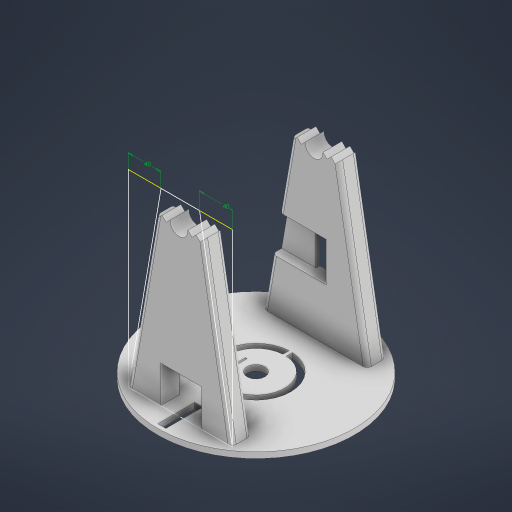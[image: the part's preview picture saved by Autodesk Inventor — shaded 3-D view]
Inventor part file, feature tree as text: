
AUTODESK INVENTOR PART (.ipt)
format: ipt  version: 2023 (Build 270158030, 158C)  size: 431,104 bytes
history: native  units: in
note: dims shown in document units (in); Inventor stores cm internally (conversion verified against a paired STEP export)
features: sketch x16, extrude x14, fillet x2, split x1
ambient origin geometry x8: Origin, YZ Plane, XZ Plane, XY Plane, X Axis, Y Axis, Z Axis, Center Point
bodies: Solid1 (feature_tree)
feature tree (33):
  extrude  "Extrusion1"  Depth=0.2756in TaperAngle=0.0deg
  extrude  "Extrusion2"  Depth=0.2756in TaperAngle=0.0deg
  sketch  "Sketch4"  dims[d10=5.0in d11=0.9055in]
  sketch  "Sketch5"  dims[d12=0.1969in d13=5.0in d14=0.9055in]
  sketch  "Sketch6"  dims[d16=2.7953in d17=9.0551in d18=0.0in]
  extrude  "Extrusion4"  Depth=0.9055in
  extrude  "Extrusion5"  Depth=0.9055in
  extrude  "Extrusion6"  Depth=9.0551in TaperAngle=0.0deg
  extrude  "Extrusion7"  Depth=1.9685in
  sketch  "Sketch9"  dims[d28=1.5748in d29=1.5748in]
  sketch  "Sketch10"  dims[d30=1.5748in d31=1.5748in]
  extrude  "Extrusion8"  Depth=1.7717in
  fillet  "Fillet1"  Radius=9.0551in
  fillet  "Fillet2"  Radius=7.2835in
  extrude  "Extrusion9"  Depth=1.5748in
  extrude  "Extrusion10"  Depth=1.5748in
  sketch  "Sketch16"  dims[d37=10.9085in d38=0.0in d39=0.2756in d40=0.0in]
  extrude  "Extrusion13"  Depth=0.1969in
  extrude  "Extrusion14"  Depth=0.1969in
  extrude  "Extrusion16"  Depth=0.2756in TaperAngle=0.0deg
  extrude  "Extrusion17"  Depth=0.3937in
  extrude  "Extrusion18"  Depth=0.3937in TaperAngle=0.0deg
  split  "Split1"
  sketch  "Sketch1"  dims[d0=9.4488in d1=0.2756in d2=0.0in]
  sketch  "Sketch2"  dims[d3=0.8583in d4=0.2756in d5=0.0in]
  sketch  "Sketch7"  dims[d19=9.0551in d20=0.0in d21=1.9685in]
  sketch  "Sketch8"  dims[d22=1.7717in d23=0.8858in d24=9.0551in d25=0.0in d26=7.2835in d27=0.0in]
  sketch  "Sketch11"  dims[d32=10.9085in d33=0.0in d34=0.1969in]
  sketch  "Sketch12"  dims[d35=0.1969in d36=0.8583in]
  sketch  "Sketch20"  dims[d51=1.7717in d52=0.3937in]
  sketch  "Sketch21"  dims[d53=2.7559in d54=0.3937in d55=0.0in]
  sketch  "Sketch22"  dims[d57=2.9528in]
  sketch  "Sketch23"  dims[d58=1.9685in d59=0.9449in d60=0.5118in d61=1.5026in d62=0.6299in d63=0.0in d66=2.7559in d67=3.3465in d68=0.0787in d69=0.0787in d70=0.0787in d71=0.4469in d72=0.0in d73=0.3346in d74=0.3346in d75=0.0787in d76=0.4469in d77=0.0in d80=1.9685in d81=1.8898in d82=0.4469in d83=0.0in d84=0.2756in d85=45.0deg d86=0.2756in d87=135.0deg d88=0.2756in d89=135.0deg d90=0.2756in d91=135.0deg d92=0.0984in d93=135.0deg d94=0.0in]
